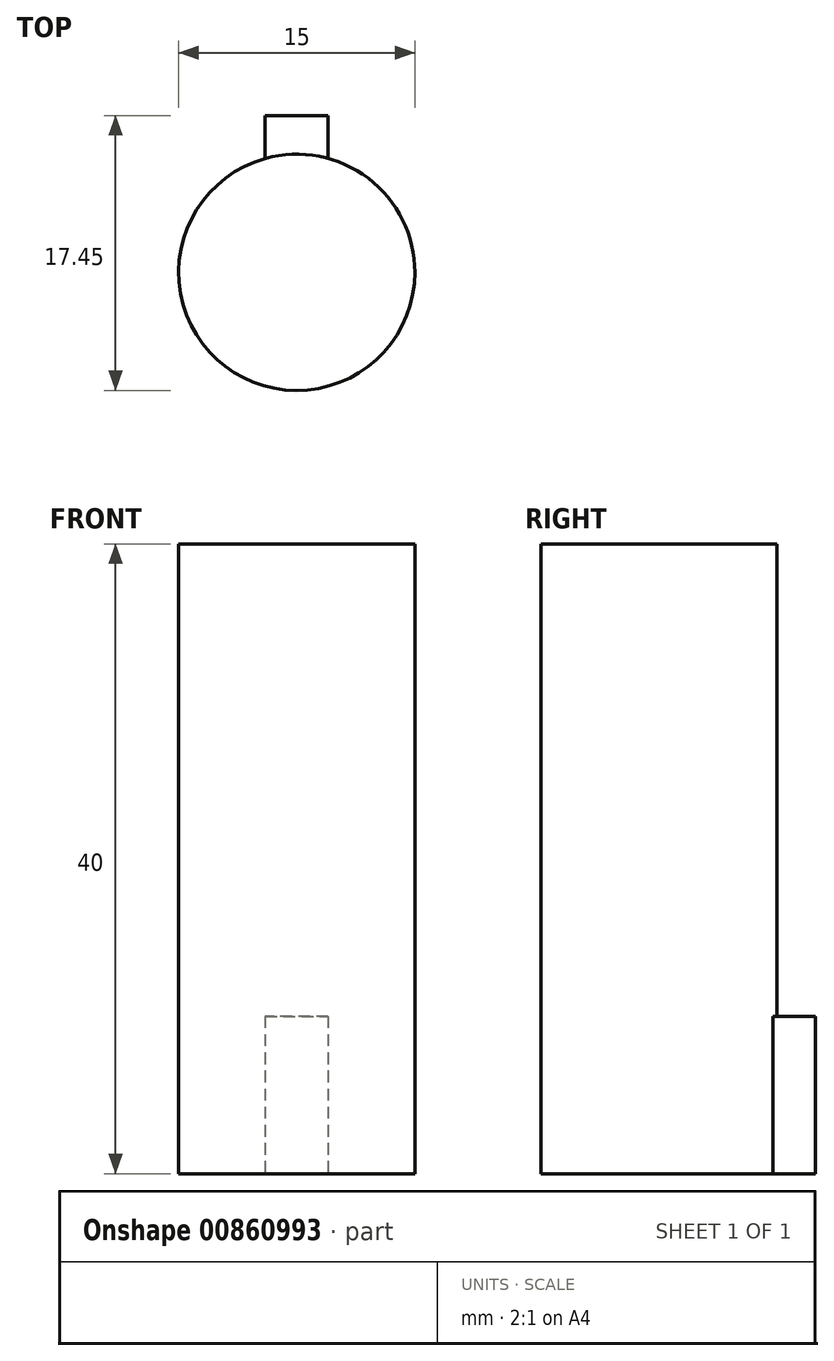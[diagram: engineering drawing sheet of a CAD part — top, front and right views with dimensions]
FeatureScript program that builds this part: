
annotation { "Feature Type Name" : "Feature", "Feature Type Description" : "" }
export const myFeature = defineFeature(function(context is Context, id is Id, definition is map)
    precondition{}
    {
        {
            var Q0;
            Q0=qCreatedBy(makeId("Top.planeOp"),FACE);
            var sketch = newSketch(context, id + "F0", { "sketchPlane" : qUnion([Q0])});
            skArc(sketch, "E0", {"start": v(-2, 7.23) * mm, "mid": v(0, -7.5) * mm, "end": v(2, 7.23) * mm});
            skLineSegment(sketch, "E1", {"start": v(-2, 7.23) * mm, "end": v(-2, 9.95) * mm});
            skLineSegment(sketch, "E2", {"start": v(-2, 9.95) * mm, "end": v(2, 9.95) * mm});
            skLineSegment(sketch, "E3", {"start": v(2, 9.95) * mm, "end": v(2, 7.23) * mm});
            skSolve(sketch);
        }
        {
            var Q0;
            Q0 = qSketchRegion(id + "F0", true);
            extrude(context, id + "F1", {"entities" : qUnion([Q0]), "depth" : 10 * mm, "offsetDistance" : 25 * mm});
        }
        {
            var Q0;
            Q0=makeQuery(id+"F1.opExtrude","CAP_FACE",FACE,{"disambiguationData":[OSD([sQuery(id+"F0.wireOp",EDGE,"E0"),sQuery(id+"F0.wireOp",EDGE,"E1"),sQuery(id+"F0.wireOp",EDGE,"E2"),sQuery(id+"F0.wireOp",EDGE,"E3")])],"isStart":false});
            var sketch = newSketch(context, id + "F2", { "sketchPlane" : qUnion([Q0])});
            skCircle(sketch, "E4", {"center": v(0, 0) * mm, "radius": 7.5 * mm});
            skSolve(sketch);
        }
        {
            var Q0;
            Q0 = qSketchRegion(id + "F2", true);
            extrude(context, id + "F3", {"entities" : qUnion([Q0]), "operationType" : NewBodyOperationType.ADD, "depth" : 30 * mm, "offsetDistance" : 25 * mm});
        }
    });
